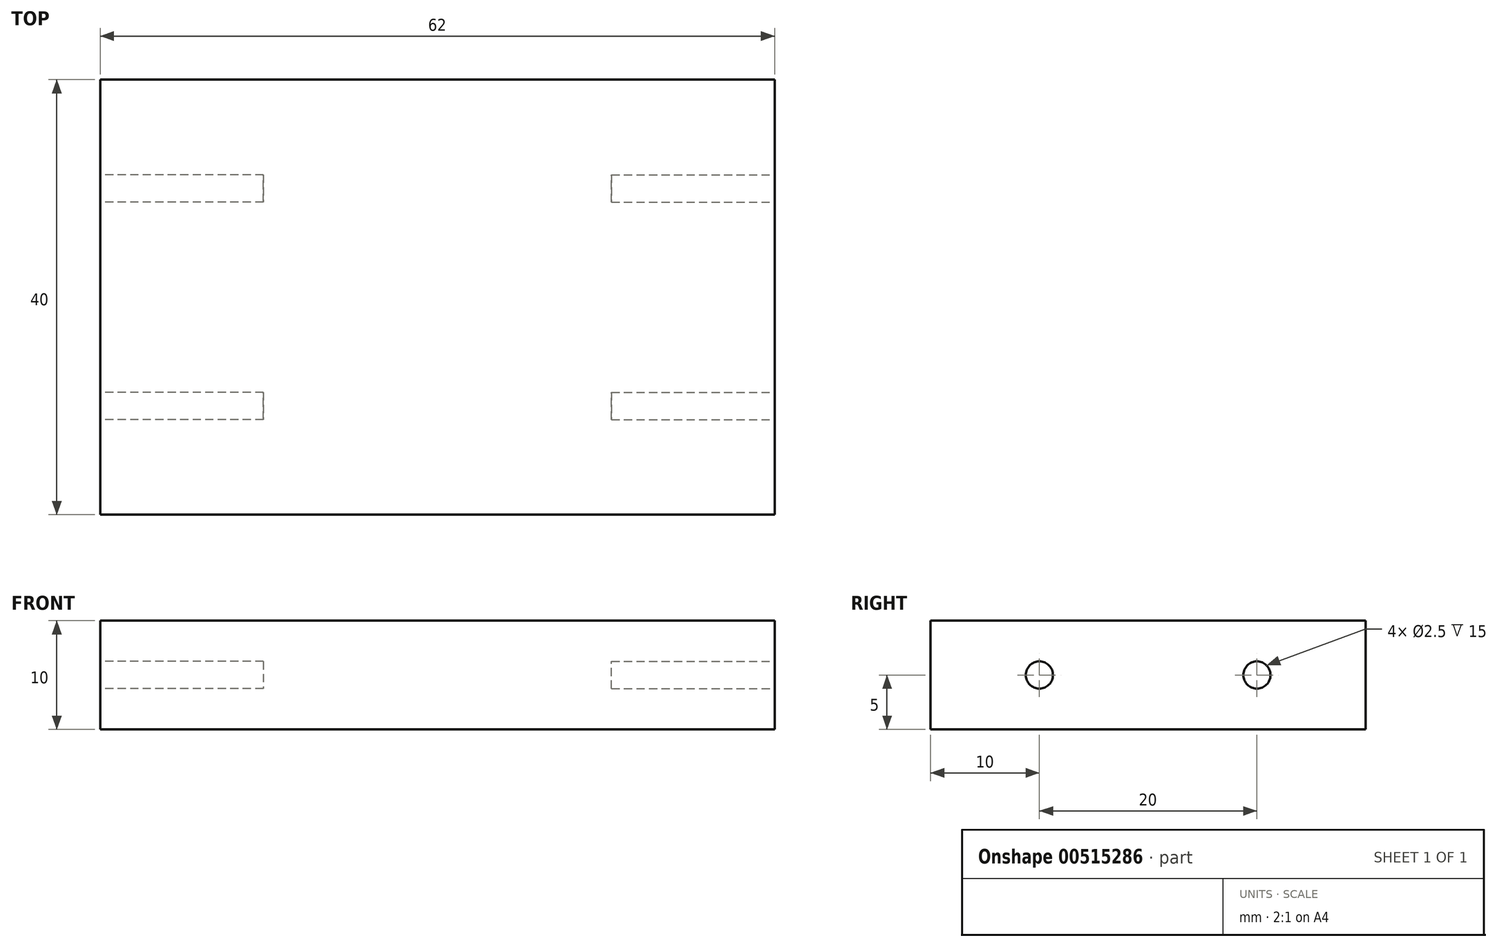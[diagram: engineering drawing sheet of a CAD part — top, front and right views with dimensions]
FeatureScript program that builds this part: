
annotation { "Feature Type Name" : "Feature", "Feature Type Description" : "" }
export const myFeature = defineFeature(function(context is Context, id is Id, definition is map)
    precondition{}
    {
        {
            var Q0;
            Q0=qCreatedBy(makeId("Top.planeOp"),FACE);
            var sketch = newSketch(context, id + "F0", { "sketchPlane" : qUnion([Q0])});
            skLineSegment(sketch, "E0.bottom", {"start": v(31, -20) * mm, "end": v(-31, -20) * mm});
            skLineSegment(sketch, "E0.top", {"start": v(31, 20) * mm, "end": v(-31, 20) * mm});
            skLineSegment(sketch, "E0.left", {"start": v(31, -20) * mm, "end": v(31, 20) * mm});
            skLineSegment(sketch, "E0.right", {"start": v(-31, -20) * mm, "end": v(-31, 20) * mm});
            skPoint(sketch, "E0.middle", {"position": v(0, 0) * mm});
            skPoint(sketch, "E1.orphan", {"position": v(16, 14) * mm});
            skPoint(sketch, "E2.orphan", {"position": v(-16, 14) * mm});
            skPoint(sketch, "E3.orphan", {"position": v(16, -14) * mm});
            skPoint(sketch, "E4.orphan", {"position": v(-16, -14) * mm});
            skPoint(sketch, "E5.visualSharp", {"position": v(-5.4, 0) * mm});
            skPoint(sketch, "E6.visualSharp", {"position": v(5.4, 0) * mm});
            skPoint(sketch, "E7.visualSharp", {"position": v(0, 3.6) * mm});
            skPoint(sketch, "E8.visualSharp", {"position": v(0, -3.6) * mm});
            skPoint(sketch, "E9.visualSharp", {"position": v(16, 7.06) * mm});
            skPoint(sketch, "E10.visualSharp", {"position": v(16, -7.06) * mm});
            skPoint(sketch, "E11.visualSharp", {"position": v(-16, 7.06) * mm});
            skPoint(sketch, "E12.visualSharp", {"position": v(-16, -7.06) * mm});
            skPoint(sketch, "E13.visualSharp", {"position": v(-15.6, 14) * mm});
            skPoint(sketch, "E14.visualSharp", {"position": v(15.6, 14) * mm});
            skPoint(sketch, "E15.visualSharp", {"position": v(15.6, -14) * mm});
            skPoint(sketch, "E16.visualSharp", {"position": v(-15.6, -14) * mm});
            skSolve(sketch);
        }
        {
            var Q0;
            Q0=makeQuery(id+"F0.imprint","IMPRINT",FACE,{"disambiguationData":[TD([[makeQuery(id+"F0.imprint","IMPRINT",EDGE,{"derivedFrom":sQuery(id+"F0.wireOp",EDGE,"E0.bottom")}),-1.0]])]});
            extrude(context, id + "F1", {"entities" : qUnion([Q0]), "depth" : 10 * mm, "offsetDistance" : 25 * mm});
        }
        {
            var Q0;
            Q0=makeQuery(id+"F1.opExtrude","SWEPT_FACE",FACE,{"disambiguationData":[OSD([sQuery(id+"F0.wireOp",EDGE,"E0.left")])]});
            var sketch = newSketch(context, id + "F2", { "sketchPlane" : qUnion([Q0])});
            skCircle(sketch, "E17", {"center": v(10, 5) * mm, "radius": 1.25 * mm});
            skCircle(sketch, "E18", {"center": v(-10, 5) * mm, "radius": 1.25 * mm});
            skSolve(sketch);
        }
        {
            var Q0;
            Q0=makeQuery(id+"F1.opExtrude","SWEPT_FACE",FACE,{"disambiguationData":[OSD([sQuery(id+"F0.wireOp",EDGE,"E0.right")])]});
            var sketch = newSketch(context, id + "F3", { "sketchPlane" : qUnion([Q0])});
            skCircle(sketch, "E19", {"center": v(-10, 5) * mm, "radius": 1.25 * mm});
            skCircle(sketch, "E20", {"center": v(10, 5) * mm, "radius": 1.25 * mm});
            skSolve(sketch);
        }
        {
            var Q0;
            Q0=makeQuery(id+"F2.imprint","IMPRINT",FACE,{"disambiguationData":[TD([[makeQuery(id+"F2.imprint","IMPRINT",EDGE,{"derivedFrom":sQuery(id+"F2.wireOp",EDGE,"E17")}),1.0]])]});
            var Q1;
            Q1=makeQuery(id+"F2.imprint","IMPRINT",FACE,{"disambiguationData":[TD([[makeQuery(id+"F2.imprint","IMPRINT",EDGE,{"derivedFrom":sQuery(id+"F2.wireOp",EDGE,"E18")}),1.0]])]});
            extrude(context, id + "F4", {"entities" : qUnion([Q0, Q1]), "operationType" : NewBodyOperationType.REMOVE, "oppositeDirection" : true, "depth" : 15 * mm, "offsetDistance" : 25 * mm});
        }
        {
            var Q0;
            Q0=makeQuery(id+"F3.imprint","IMPRINT",FACE,{"disambiguationData":[TD([[makeQuery(id+"F3.imprint","IMPRINT",EDGE,{"derivedFrom":sQuery(id+"F3.wireOp",EDGE,"E19")}),1.0]])]});
            var Q1;
            Q1=makeQuery(id+"F3.imprint","IMPRINT",FACE,{"disambiguationData":[TD([[makeQuery(id+"F3.imprint","IMPRINT",EDGE,{"derivedFrom":sQuery(id+"F3.wireOp",EDGE,"E20")}),1.0]])]});
            extrude(context, id + "F5", {"entities" : qUnion([Q0, Q1]), "operationType" : NewBodyOperationType.REMOVE, "oppositeDirection" : true, "depth" : 15 * mm, "offsetDistance" : 25 * mm});
        }
    });
